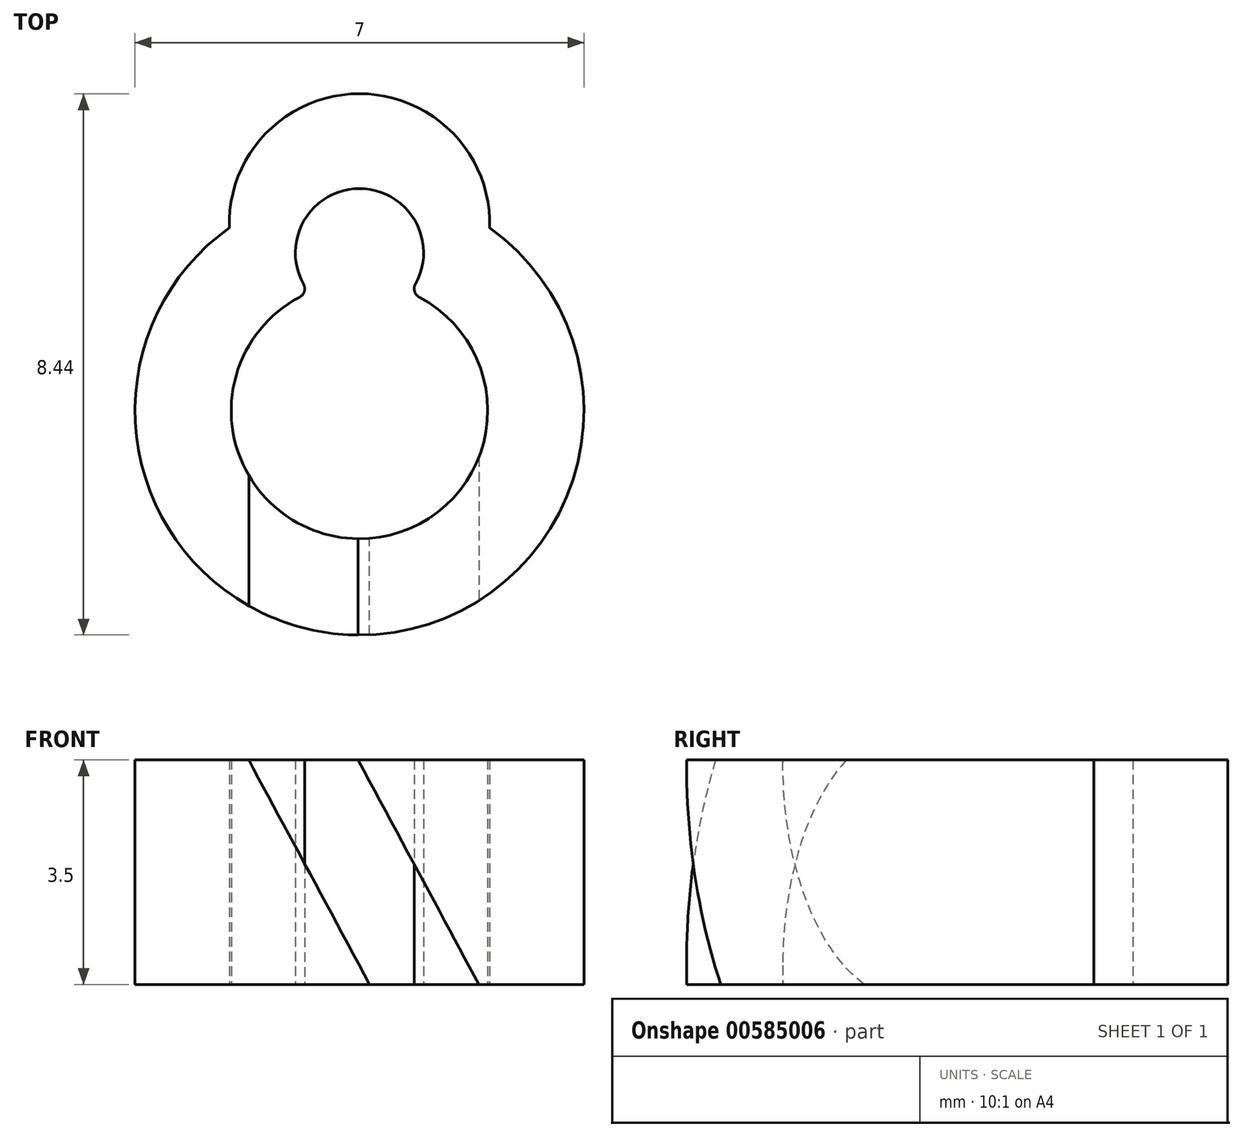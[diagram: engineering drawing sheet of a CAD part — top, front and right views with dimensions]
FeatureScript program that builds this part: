
annotation { "Feature Type Name" : "Feature", "Feature Type Description" : "" }
export const myFeature = defineFeature(function(context is Context, id is Id, definition is map)
    precondition{}
    {
        {
            var Q0;
            Q0=qCreatedBy(makeId("Top.planeOp"),FACE);
            var sketch = newSketch(context, id + "F0", { "sketchPlane" : qUnion([Q0])});
            skArc(sketch, "E0", {"start": v(-0.78, 1.84) * mm, "mid": v(0, -2) * mm, "end": v(0.78, 1.84) * mm});
            skArc(sketch, "E1", {"start": v(0.78, 1.84) * mm, "mid": v(0, 3.46) * mm, "end": v(-0.78, 1.84) * mm});
            skArc(sketch, "E2", {"start": v(-2.03, 2.85) * mm, "mid": v(0, -3.5) * mm, "end": v(2.03, 2.85) * mm});
            skArc(sketch, "E3.trimOffspring", {"start": v(2.03, 2.85) * mm, "mid": v(0, 4.94) * mm, "end": v(-2.03, 2.85) * mm});
            skCircle(sketch, "E4", {"center": v(-6.72, 1.68) * mm, "radius": 1.71 * mm});
            skSolve(sketch);
        }
        {
            var Q0;
            Q0=makeQuery(id+"F0.imprint","IMPRINT",FACE,{"disambiguationData":[TD([[makeQuery(id+"F0.imprint","IMPRINT",EDGE,{"derivedFrom":sQuery(id+"F0.wireOp",EDGE,"E0")}),-1.0]])]});
            extrude(context, id + "F1", {"entities" : qUnion([Q0]), "depth" : 3.5 * mm, "offsetDistance" : 25 * mm});
        }
        {
            var Q0;
            {var subQ0=sQuery(id+"F0.wireOp",EDGE,"E1");var subQ1=sQuery(id+"F0.wireOp",EDGE,"E0");Q0=makeQuery(id+"F1.opExtrude","SWEPT_EDGE",EDGE,{"disambiguationData":[OSD([subQ1,subQ0]),TDD([makeQuery(id+"F0.imprint","INTERSECT",VERTEX,{"disambiguationData":[OD(0.0)],"derivedFrom":[subQ1,subQ0]})])]});}
            var Q1;
            {var subQ0=sQuery(id+"F0.wireOp",EDGE,"E1");var subQ1=sQuery(id+"F0.wireOp",EDGE,"E0");Q1=makeQuery(id+"F1.opExtrude","SWEPT_EDGE",EDGE,{"disambiguationData":[OSD([subQ1,subQ0]),TDD([makeQuery(id+"F0.imprint","INTERSECT",VERTEX,{"disambiguationData":[OD(1.0)],"derivedFrom":[subQ1,subQ0]})])]});}
            fillet(context, id + "F2", {"entities" : qUnion([Q0, Q1]), "radius" : .15 * mm, "tangentPropagation" : true, "allowEdgeOverflow" : false});
        }
        {
            var Q0;
            Q0=qCreatedBy(makeId("Front.planeOp"),FACE);
            var sketch = newSketch(context, id + "F3", { "sketchPlane" : qUnion([Q0])});
            skLineSegment(sketch, "E5", {"start": v(-4.24, 8.17) * mm, "end": v(3.13, -5.51) * mm});
            skLineSegment(sketch, "E6", {"start": v(3.13, -5.51) * mm, "end": v(4.83, -5.51) * mm});
            skLineSegment(sketch, "E7", {"start": v(4.83, -5.51) * mm, "end": v(-2.6, 8.29) * mm});
            skLineSegment(sketch, "E8", {"start": v(-2.6, 8.29) * mm, "end": v(-4.24, 8.17) * mm});
            skSolve(sketch);
        }
        {
            var Q0;
            Q0=makeQuery(id+"F3.imprint","IMPRINT",FACE,{"disambiguationData":[TD([[makeQuery(id+"F3.imprint","IMPRINT",EDGE,{"derivedFrom":sQuery(id+"F3.wireOp",EDGE,"E5")}),1.0]])]});
            extrude(context, id + "F4", {"entities" : qUnion([Q0]), "operationType" : NewBodyOperationType.REMOVE, "depth" : 25 * mm, "offsetDistance" : 25 * mm});
        }
    });
